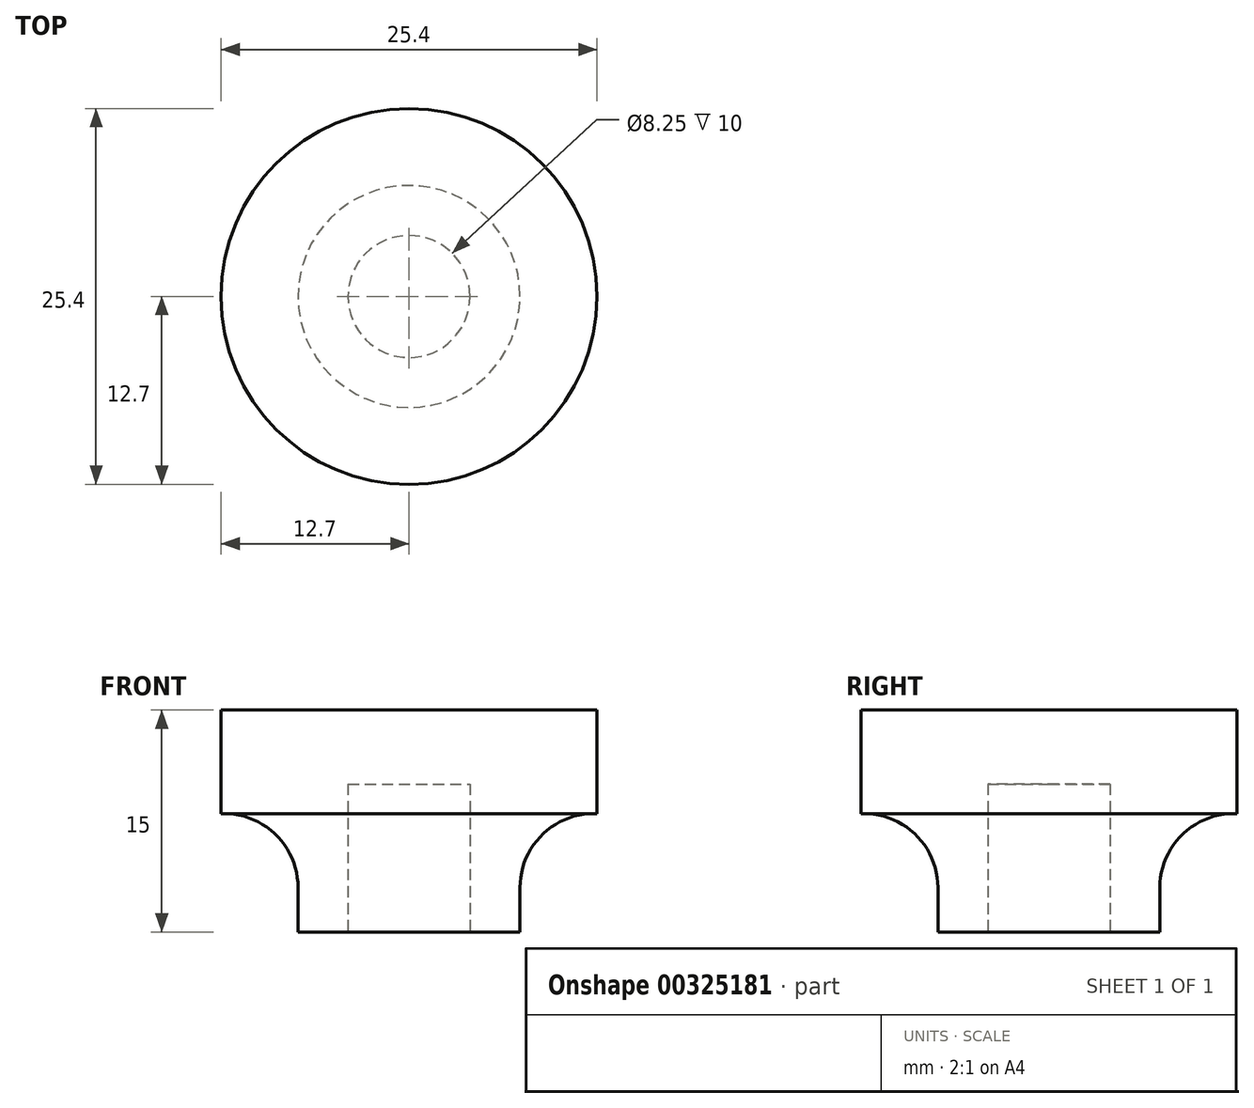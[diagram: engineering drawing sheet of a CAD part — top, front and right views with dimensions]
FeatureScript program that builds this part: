
annotation { "Feature Type Name" : "Feature", "Feature Type Description" : "" }
export const myFeature = defineFeature(function(context is Context, id is Id, definition is map)
    precondition{}
    {
        {
            var Q0;
            Q0=qCreatedBy(makeId("Top.planeOp"),FACE);
            var sketch = newSketch(context, id + "F0", { "sketchPlane" : qUnion([Q0])});
            skCircle(sketch, "E0", {"center": v(0, 0) * mm, "radius": 12.7 * mm});
            skSolve(sketch);
        }
        {
            var Q0;
            Q0 = qSketchRegion(id + "F0", true);
            extrude(context, id + "F1", {"entities" : qUnion([Q0]), "depth" : 15 * mm});
        }
        {
            var Q0;
            Q0=makeQuery(id+"F1.opExtrude","CAP_FACE",FACE,{"disambiguationData":[OSD([sQuery(id+"F0.wireOp",EDGE,"E0")])],"isStart":true});
            var sketch = newSketch(context, id + "F2", { "sketchPlane" : qUnion([Q0])});
            skCircle(sketch, "E1", {"center": v(0, 0) * mm, "radius": 4.12 * mm});
            skSolve(sketch);
        }
        {
            var Q0;
            Q0 = qSketchRegion(id + "F2", true);
            extrude(context, id + "F3", {"entities" : qUnion([Q0]), "operationType" : NewBodyOperationType.REMOVE, "oppositeDirection" : true, "depth" : 10 * mm});
        }
        {
            var Q0;
            Q0=makeQuery(id+"F1.opExtrude","CAP_FACE",FACE,{"disambiguationData":[OSD([sQuery(id+"F0.wireOp",EDGE,"E0")])],"isStart":true});
            var sketch = newSketch(context, id + "F4", { "sketchPlane" : qUnion([Q0])});
            skCircle(sketch, "E2", {"center": v(0, 0) * mm, "radius": 7.5 * mm});
            skCircle(sketch, "E3", {"center": v(0, 0) * mm, "radius": 12.7 * mm});
            skSolve(sketch);
        }
        {
            var Q0;
            Q0 = qSketchRegion(id + "F4", true);
            extrude(context, id + "F5", {"entities" : qUnion([Q0]), "operationType" : NewBodyOperationType.REMOVE, "oppositeDirection" : true, "depth" : 8 * mm});
        }
        {
            var Q0;
            Q0=makeQuery(id+"F5.boolean.opBoolean","COPY",EDGE,{"derivedFrom":makeQuery(id+"F5.opExtrude","CAP_EDGE",EDGE,{"disambiguationData":[OSD([sQuery(id+"F4.wireOp",EDGE,"E2")])],"isStart":false})});
            fillet(context, id + "F6", {"entities" : qUnion([Q0]), "radius" : 5 * mm, "tangentPropagation" : true, "allowEdgeOverflow" : false});
        }
    });
